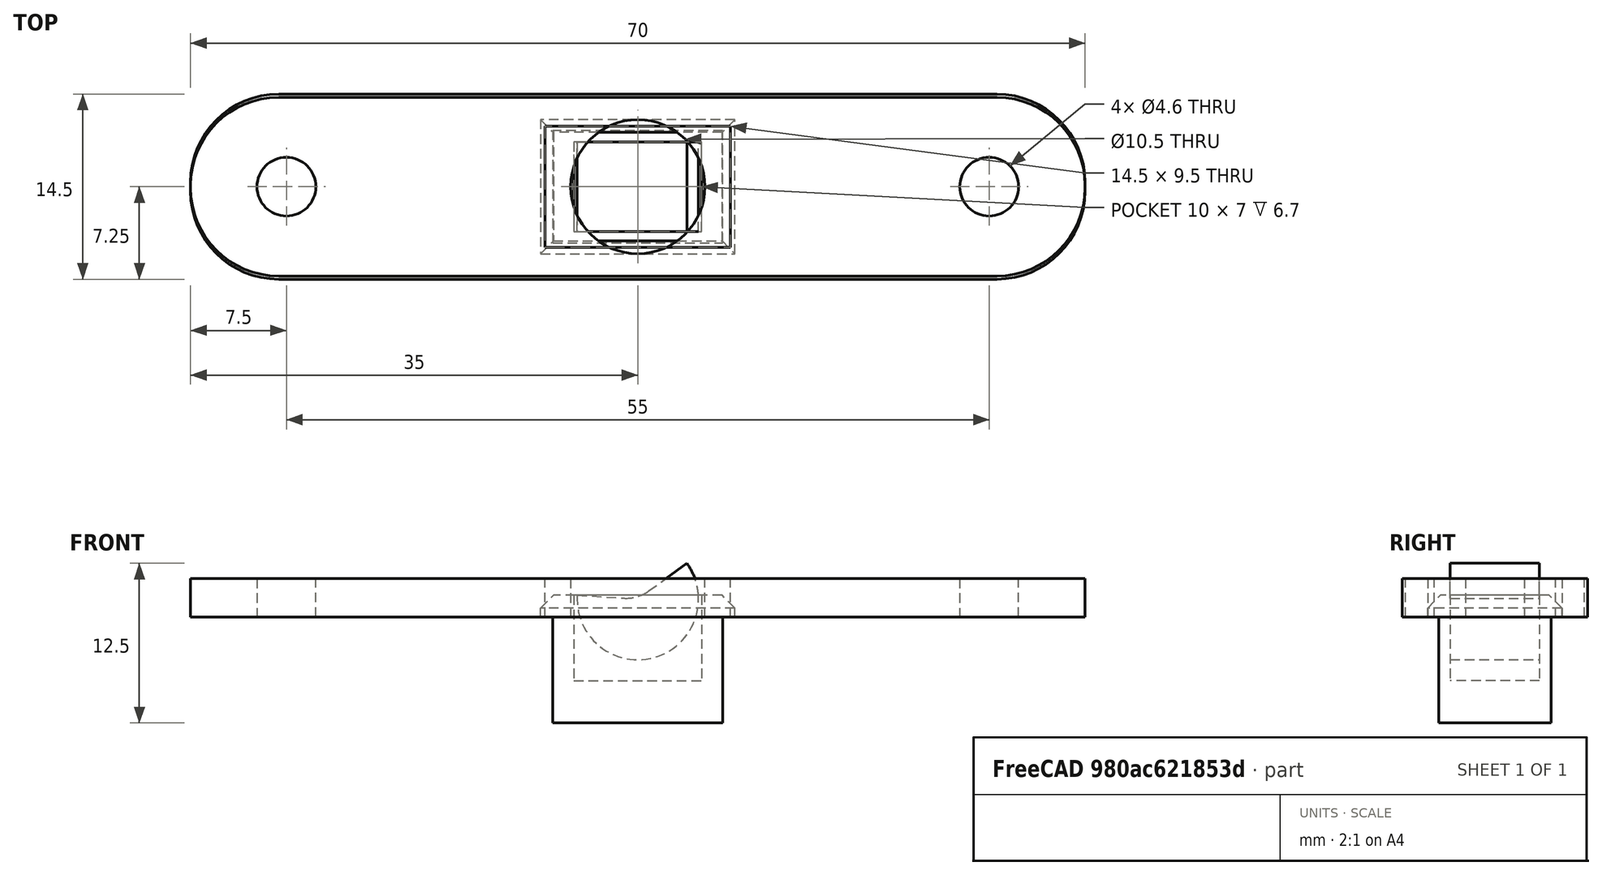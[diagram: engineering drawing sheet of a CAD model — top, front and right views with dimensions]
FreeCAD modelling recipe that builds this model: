
FCSTD DOCUMENT  (FreeCAD 1.0R38641 +678 (Git))
Label: button
License: All rights reserved
LicenseURL: https://en.wikipedia.org/wiki/All_rights_reserved
objects: Sketcher::SketchObject×6, PartDesign::Pad×5, PartDesign::Body×3, PartDesign::Fillet×2, Mesh::Feature×2, PartDesign::Pocket×1, PartDesign::Chamfer×1, App::Part×1
note: 42 computed .brp shape members not serialized (recipe doc carries the construction recipe); baked Part::Feature solids carry a one-line shape summary decoded from their .brp

FEATURE [Sketcher::SketchObject] Sketch
  ArcFitTolerance = 1e-06
  AttachmentSupport = -> [XY_Plane]
  FullyConstrained = true
  MakeInternals = false
  MapMode = 5
  sketch-geometry (4):
    g0: LineSegment StartX=-7.6 StartY=5.25 StartZ=0 EndX=-7.6 EndY=-5.25 EndZ=0
    g1: LineSegment StartX=-7.6 StartY=-5.25 StartZ=0 EndX=7.6 EndY=-5.25 EndZ=0
    g2: LineSegment StartX=7.6 StartY=-5.25 StartZ=0 EndX=7.6 EndY=5.25 EndZ=0
    g3: LineSegment StartX=7.6 StartY=5.25 StartZ=0 EndX=-7.6 EndY=5.25 EndZ=0
  constraints (11):
    c: Coincident(g0,g1)
    c: Coincident(g1,g2)
    c: Coincident(g2,g3)
    c: Coincident(g3,g0)
    c: Vertical(g0)
    c: Vertical(g2)
    c: Horizontal(g1)
    c: Horizontal(g3)
    c: Symmetric(g1,g0,g-1)
    c: DistanceY(g0,g0) = 10.5
    c: DistanceX(g3,g3) = 15.2
FEATURE [PartDesign::Pad] Pad
  Direction = (0,0,1)
  Length = 1.7
  Length2 = 10
  Profile = -> Sketch
  ReferenceAxis = -> Sketch [N_Axis]
  Refine = true
  Suppressed = false
  Type = 0
FEATURE [Sketcher::SketchObject] Sketch001
  ArcFitTolerance = 1e-06
  AttachmentSupport = -> [XY_Plane]
  FullyConstrained = true
  MakeInternals = false
  MapMode = 5
  sketch-geometry (4):
    g0: LineSegment StartX=-6.65 StartY=4.4 StartZ=0 EndX=-6.65 EndY=-4.4 EndZ=0
    g1: LineSegment StartX=-6.65 StartY=-4.4 StartZ=0 EndX=6.65 EndY=-4.4 EndZ=0
    g2: LineSegment StartX=6.65 StartY=-4.4 StartZ=0 EndX=6.65 EndY=4.4 EndZ=0
    g3: LineSegment StartX=6.65 StartY=4.4 StartZ=0 EndX=-6.65 EndY=4.4 EndZ=0
  constraints (11):
    c: Coincident(g0,g1)
    c: Coincident(g1,g2)
    c: Coincident(g2,g3)
    c: Coincident(g3,g0)
    c: Vertical(g0)
    c: Vertical(g2)
    c: Horizontal(g1)
    c: Horizontal(g3)
    c: Symmetric(g2,g0,g-1)
    c: DistanceY(g2,g2) = 8.8
    c: DistanceX(g3,g3) = 13.3
FEATURE [PartDesign::Pad] Pad001
  BaseFeature = -> Pad
  Direction = (0,0,1)
  Length = 8.3
  Length2 = 10
  Profile = -> Sketch001
  ReferenceAxis = -> Sketch001 [N_Axis]
  Refine = true
  Reversed = true
  Suppressed = false
  Type = 0
FEATURE [Sketcher::SketchObject] Sketch002
  ArcFitTolerance = 1e-06
  AttachmentSupport = -> [XY_Plane]
  FullyConstrained = true
  MakeInternals = false
  MapMode = 5
  sketch-geometry (4):
    g0: LineSegment StartX=-5 StartY=3.5 StartZ=0 EndX=-5 EndY=-3.5 EndZ=0
    g1: LineSegment StartX=-5 StartY=-3.5 StartZ=0 EndX=5 EndY=-3.5 EndZ=0
    g2: LineSegment StartX=5 StartY=-3.5 StartZ=0 EndX=5 EndY=3.5 EndZ=0
    g3: LineSegment StartX=5 StartY=3.5 StartZ=0 EndX=-5 EndY=3.5 EndZ=0
  constraints (11):
    c: Coincident(g0,g1)
    c: Coincident(g1,g2)
    c: Coincident(g2,g3)
    c: Coincident(g3,g0)
    c: Vertical(g0)
    c: Vertical(g2)
    c: Horizontal(g1)
    c: Horizontal(g3)
    c: DistanceX(g3,g3) = 10
    c: DistanceY(g0,g0) = 7
    c: Symmetric(g0,g1,g-1)
FEATURE [PartDesign::Pocket] Pocket
  BaseFeature = -> Pad001
  Direction = (0,0,-1)
  Length = 10
  Length2 = 5
  Midplane = true
  Profile = -> Sketch002
  ReferenceAxis = -> Sketch002 [N_Axis]
  Refine = true
  Suppressed = false
  Type = 0
FEATURE [Sketcher::SketchObject] Sketch003
  ArcFitTolerance = 1e-06
  AttachmentSupport = -> [Pocket]
  FullyConstrained = true
  MakeInternals = false
  MapMode = 5
  Placement = pos=(0,3.5,0) rot=(1,0,0;1.5708rad)
  sketch-geometry (5):
    g0: ArcOfCircle CenterX=0 CenterY=1.4 CenterZ=0 NormalX=0 NormalY=0 NormalZ=1 AngleXU=0 Radius=4.75 StartAngle=3.07839 EndAngle=6.91359
    g1: LineSegment StartX=-4.74052 StartY=1.7 StartZ=0 EndX=-1.08207 EndY=1.46848 EndZ=0
    g2: LineSegment StartX=0.875828 StartY=2.03913 StartZ=0 EndX=3.83699 EndY=4.2 EndZ=0
    g3: ArcOfCircle CenterX=-0.892593 CenterY=4.46249 CenterZ=0 NormalX=0 NormalY=0 NormalZ=1 AngleXU=0 Radius=3 StartAngle=4.64919 EndAngle=5.3428
    g4: GeomPoint [constr] X=0 Y=1.4 Z=0
  constraints (13):
    c: Coincident(g1,g0)
    c: Coincident(g4,g0)
    c: PointOnObject(g0,g-2)
    c: Coincident(g2,g0)
    c: Diameter(g0) = 9.5
    c: DistanceY(g-1,g0) = 1.4
    c: DistanceY(g-1,g0) = 4.2
    c: DistanceY(g-1,g0) = 1.7
    c: PointOnObject(g4,g1)
    c: PointOnObject(g4,g2)
    c: Tangent(g1,g3) = -1.5708
    c: Tangent(g2,g3) = -1.5708
    c: Diameter(g3) = 6
FEATURE [PartDesign::Pad] Pad002
  BaseFeature = -> Pocket
  Direction = (0,-1,2e-16)
  Length = 7
  Length2 = 10
  Profile = -> Sketch003
  ReferenceAxis = -> Sketch003 [N_Axis]
  Refine = true
  Suppressed = false
  Type = 0
FEATURE [PartDesign::Chamfer] Chamfer
  Angle = 45
  Base = -> Pad002 [Edge4,Edge7,Edge16,Edge10]
  BaseFeature = -> Pad002
  ChamferType = 0
  FlipDirection = false
  Refine = true
  Size = 1
  Size2 = 1
  SupportTransform = false
  Suppressed = false
  UseAllEdges = false
FEATURE [PartDesign::Body] Body  label="Body_Button"
  AllowCompound = false
  Group = -> [Sketch,Pad,Sketch001,Pad001,Sketch002,Pocket,Sketch003,Pad002,Chamfer]
  Origin = -> Origin
  Tip = -> Chamfer
FEATURE [Sketcher::SketchObject] Sketch004
  ArcFitTolerance = 1e-06
  AttachmentSupport = -> [XY_Plane001]
  FullyConstrained = true
  MakeInternals = false
  MapMode = 5
  sketch-geometry (10):
    g0: LineSegment StartX=-35 StartY=7 StartZ=0 EndX=-35 EndY=-7 EndZ=0
    g1: LineSegment StartX=-35 StartY=-7 StartZ=0 EndX=35 EndY=-7 EndZ=0
    g2: LineSegment StartX=35 StartY=-7 StartZ=0 EndX=35 EndY=7 EndZ=0
    g3: LineSegment StartX=35 StartY=7 StartZ=0 EndX=-35 EndY=7 EndZ=0
    g4: Circle CenterX=-27.5 CenterY=0 CenterZ=0 NormalX=0 NormalY=0 NormalZ=1 AngleXU=0 Radius=2.3
    g5: Circle CenterX=27.5 CenterY=0 CenterZ=0 NormalX=0 NormalY=0 NormalZ=1 AngleXU=0 Radius=2.3
    g6: LineSegment StartX=-7.25 StartY=4.75 StartZ=0 EndX=-7.25 EndY=-4.75 EndZ=0
    g7: LineSegment StartX=-7.25 StartY=-4.75 StartZ=0 EndX=7.25 EndY=-4.75 EndZ=0
    g8: LineSegment StartX=7.25 StartY=-4.75 StartZ=0 EndX=7.25 EndY=4.75 EndZ=0
    g9: LineSegment StartX=7.25 StartY=4.75 StartZ=0 EndX=-7.25 EndY=4.75 EndZ=0
  constraints (27):
    c: Coincident(g0,g1)
    c: Coincident(g1,g2)
    c: Coincident(g2,g3)
    c: Coincident(g3,g0)
    c: Vertical(g0)
    c: Vertical(g2)
    c: Horizontal(g1)
    c: Horizontal(g3)
    c: Symmetric(g0,g1,g-1)
    c: PointOnObject(g4,g-1)
    c: Symmetric(g4,g5,g-2)
    c: DistanceX(g4,g5) = 55
    c: DistanceX(g3,g3) = 70
    c: DistanceY(g0,g0) = 14
    c: Equal(g4,g5)
    c: Diameter(g4) = 4.6
    c: Coincident(g6,g7)
    c: Coincident(g7,g8)
    c: Coincident(g8,g9)
    c: Coincident(g9,g6)
    c: Vertical(g6)
    c: Vertical(g8)
    c: Horizontal(g7)
    c: Horizontal(g9)
    c: Symmetric(g6,g7,g-1)
    c: DistanceY(g6,g6) = 9.5
    c: DistanceX(g9,g9) = 14.5
FEATURE [PartDesign::Pad] Pad003
  Direction = (0,0,1)
  Length = 3
  Length2 = 10
  Profile = -> Sketch004
  ReferenceAxis = -> Sketch004 [N_Axis]
  Refine = true
  Suppressed = false
  Type = 0
FEATURE [PartDesign::Fillet] Fillet
  Base = -> Pad003 [Edge1,Edge2,Edge8,Edge5]
  BaseFeature = -> Pad003
  Radius = 6.9
  Refine = true
  SupportTransform = false
  Suppressed = false
  UseAllEdges = false
FEATURE [PartDesign::Body] Body001  label="Body_button_handle"
  AllowCompound = false
  Group = -> [Sketch004,Pad003,Fillet]
  Origin = -> Origin001
  Tip = -> Fillet
FEATURE [Mesh::Feature] Mesh  label="Body_button_handle (Meshed)"
FEATURE [App::Part] Part
  Origin = -> Origin002
FEATURE [Sketcher::SketchObject] Sketch005
  ArcFitTolerance = 1e-06
  AttachmentSupport = -> [XY_Plane003]
  FullyConstrained = true
  MakeInternals = false
  MapMode = 5
  sketch-geometry (7):
    g0: LineSegment StartX=-35 StartY=7.25 StartZ=0 EndX=-35 EndY=-7.25 EndZ=0
    g1: LineSegment StartX=-35 StartY=-7.25 StartZ=0 EndX=35 EndY=-7.25 EndZ=0
    g2: LineSegment StartX=35 StartY=-7.25 StartZ=0 EndX=35 EndY=7.25 EndZ=0
    g3: LineSegment StartX=35 StartY=7.25 StartZ=0 EndX=-35 EndY=7.25 EndZ=0
    g4: Circle CenterX=-27.5 CenterY=0 CenterZ=0 NormalX=0 NormalY=0 NormalZ=1 AngleXU=0 Radius=2.3
    g5: Circle CenterX=27.5 CenterY=0 CenterZ=0 NormalX=0 NormalY=0 NormalZ=1 AngleXU=0 Radius=2.3
    g6: Circle CenterX=0 CenterY=0 CenterZ=0 NormalX=0 NormalY=0 NormalZ=1 AngleXU=0 Radius=5.25
  constraints (18):
    c: Coincident(g0,g1)
    c: Coincident(g1,g2)
    c: Coincident(g2,g3)
    c: Coincident(g3,g0)
    c: Vertical(g0)
    c: Vertical(g2)
    c: Horizontal(g1)
    c: Horizontal(g3)
    c: Symmetric(g0,g1,g-1)
    c: PointOnObject(g4,g-1)
    c: Symmetric(g4,g5,g-2)
    c: DistanceX(g4,g5) = 55
    c: DistanceX(g3,g3) = 70
    c: DistanceY(g0,g0) = 14.5
    c: Equal(g4,g5)
    c: Diameter(g4) = 4.6
    c: Coincident(g6,g-1)
    c: Diameter(g6) = 10.5
FEATURE [PartDesign::Pad] Pad004
  Direction = (0,0,1)
  Length = 3
  Length2 = 10
  Profile = -> Sketch005
  ReferenceAxis = -> Sketch005 [N_Axis]
  Refine = true
  Suppressed = false
  Type = 0
FEATURE [PartDesign::Fillet] Fillet001
  Base = -> Pad004 [Edge1,Edge2,Edge8,Edge5]
  BaseFeature = -> Pad004
  Radius = 6.9
  Refine = true
  SupportTransform = false
  Suppressed = false
  UseAllEdges = false
FEATURE [PartDesign::Body] Body002  label="Body_button_handle_Hole"
  AllowCompound = false
  Group = -> [Sketch005,Pad004,Fillet001]
  Origin = -> Origin003
  Tip = -> Fillet001
FEATURE [Mesh::Feature] Mesh001  label="Body_button_handle_Hole (Meshed)"
